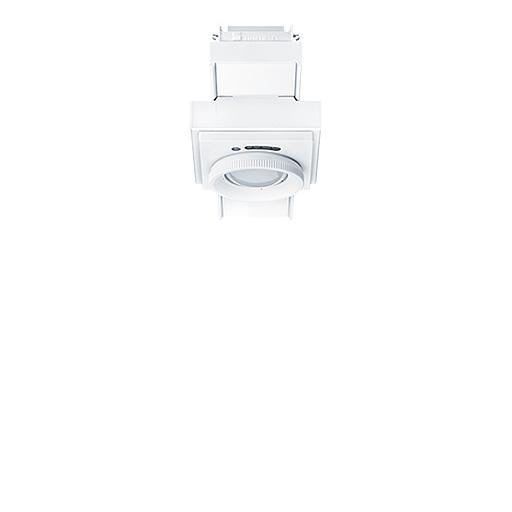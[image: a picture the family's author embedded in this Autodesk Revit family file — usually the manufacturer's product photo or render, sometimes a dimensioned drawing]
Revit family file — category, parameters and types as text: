
# Revit family: Zumtobel TECTON 2 motion and daylight sensors
name_source: partatom
category: Lighting Devices
units: mm (PartAtom-declared; Revit-internal decimal feet)

## family parameters
Cut with Voids When Loaded = No
Host = Face
Maintain Annotation Orientation = No
Part Type = Normal
Room Calculation Point = Yes
Round Connector Dimension = Use Diameter
Shared = Yes

## types (6) — shared parameters
Description = Lighting and occupancy sensors
Export Type to IFC As = IfcSensorType
Luminaire Height = 90 mm
Luminaire Length = 250 mm
Luminaire Width = 60 mm
Manufacturer = Zumtobel Lighting
Type IFC Predefined Type = MOVEMENTSENSOR
zero-valued in all types: Default Elevation

## per-type parameters (varying)
| type | Assembly Code | Material Body | Material Housing | Model | Type Image | URL | Visibility HC | Visibility LC/MC |
| DALI MSENS HC TEC2 WH | Pr_75_75_27_23 | Zumtobel-Plastic-RAL 9003-Signal White | Zumtobel-Plastic-RAL 9003-Signal White | 22172957 | ZS_TEC_F_MSENS_HC_WH.jpg | www.zumtobel.com/22172957 | Yes | No |
| DALI MSENS HC TEC2 BK | Pr_75_50_76_58 | Zumtobel-Plastic-RAL 9003-Signal White | Zumtobel-Plastic-RAL 9005-Jet Black | 22173116 | ZS_TEC_F_MSENS_HC_BK.jpg | www.zumtobel.com/22173116 | Yes | No |
| DALI MSENS LC TEC2 WH | Pr_75_75_27_23 | Zumtobel-Plastic-RAL 9003-Signal White | Zumtobel-Plastic-RAL 9003-Signal White | 22172964 | ZS_TE2_F_MSENS_MC_WH.jpg | www.zumtobel.com/22172964 | No | Yes |
| DALI MSENS LC TEC2 BK | Pr_75_75_27_23 | Zumtobel-Plastic-RAL 9005-Jet Black | Zumtobel-Plastic-RAL 9005-Jet Black | 22173118 | ZS_TE2_F_MSENS_MC_BK.jpg | www.zumtobel.com/22173118 | No | Yes |
| DALI MSENS MC TEC2 BK | Pr_75_75_27_23 | Zumtobel-Plastic-RAL 9005-Jet Black | Zumtobel-Plastic-RAL 9005-Jet Black | 22173120 | ZS_TE2_F_MSENS_MC_BK.jpg | www.zumtobel.com/22173120 | No | Yes |
| DALI MSENS MC TEC2 WH | Pr_75_75_27_23 | Zumtobel-Plastic-RAL 9003-Signal White | Zumtobel-Plastic-RAL 9003-Signal White | 22172956 | ZS_TE2_F_MSENS_MC_WH.jpg | www.zumtobel.com/22172956 | No | Yes |

## geometry (parser evidence)
native form markers: Sweep x3
no freeform markers — native parametric forms only
